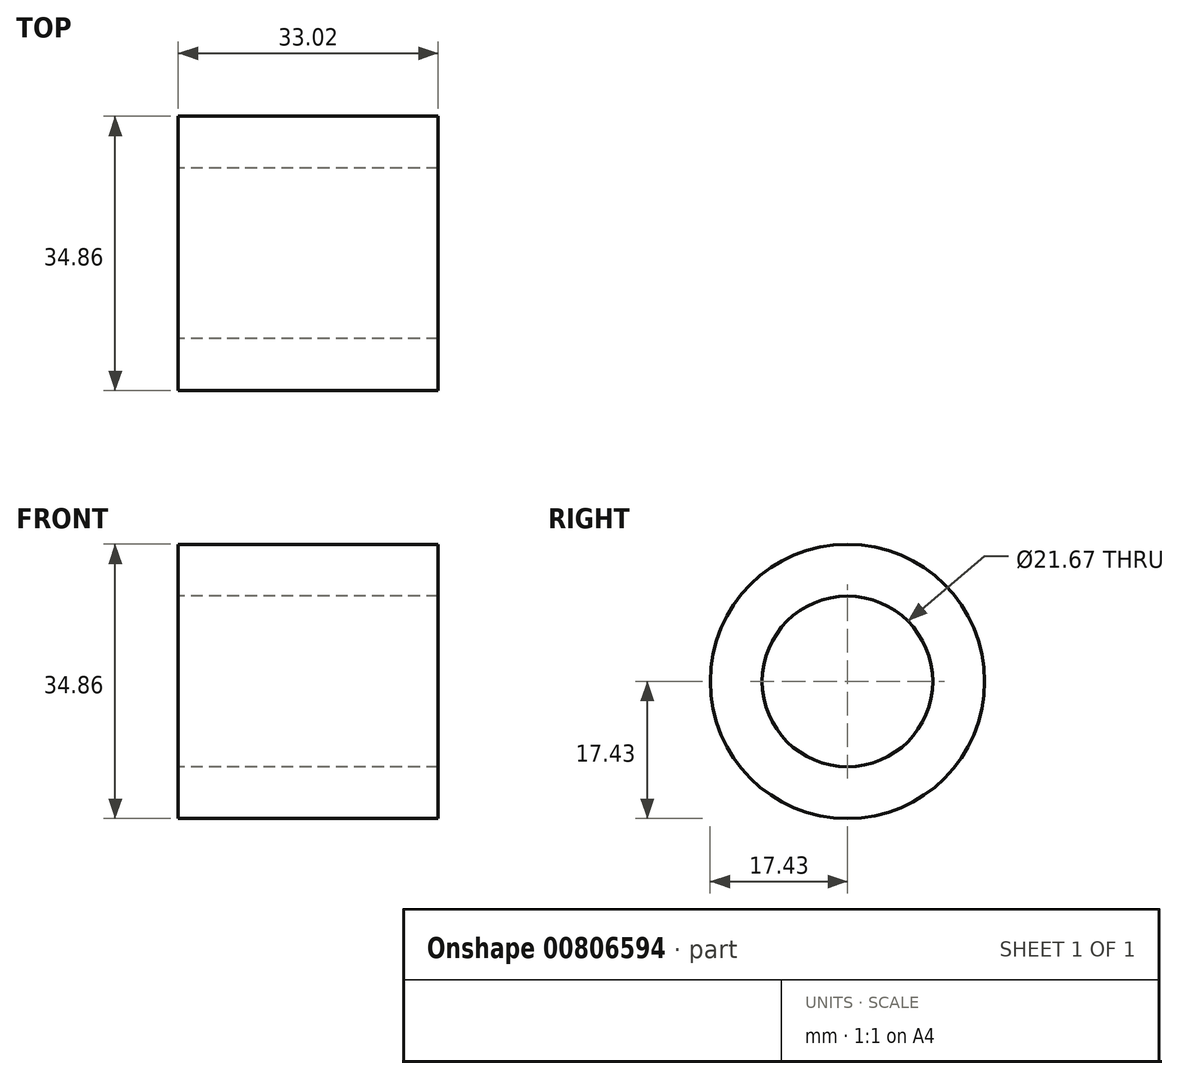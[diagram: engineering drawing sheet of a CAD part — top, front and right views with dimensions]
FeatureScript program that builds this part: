
annotation { "Feature Type Name" : "Feature", "Feature Type Description" : "" }
export const myFeature = defineFeature(function(context is Context, id is Id, definition is map)
    precondition{}
    {
        {
            var Q0;
            Q0=qCreatedBy(makeId("Right.planeOp"),FACE);
            var sketch = newSketch(context, id + "F0", { "sketchPlane" : qUnion([Q0])});
            skCircle(sketch, "E0", {"center": v(0, 0) * mm, "radius": 17.43 * mm});
            skCircle(sketch, "E1", {"center": v(0, 0) * mm, "radius": 10.83 * mm});
            skSolve(sketch);
        }
        {
            var Q0;
            Q0 = qSketchRegion(id + "F0", true);
            extrude(context, id + "F1", {"entities" : qUnion([Q0]), "depth" : 7.62 * mm, "offsetDistance" : 25.4 * mm});
        }
        {
            var Q0;
            Q0=makeQuery(id+"F1.opExtrude","CAP_FACE",FACE,{"disambiguationData":[OSD([sQuery(id+"F0.wireOp",EDGE,"E0"),sQuery(id+"F0.wireOp",EDGE,"E1")])],"isStart":false});
            extrude(context, id + "F2", {"entities" : qUnion([Q0]), "operationType" : NewBodyOperationType.ADD, "depth" : 25.4 * mm, "offsetDistance" : 25.4 * mm});
        }
    });
